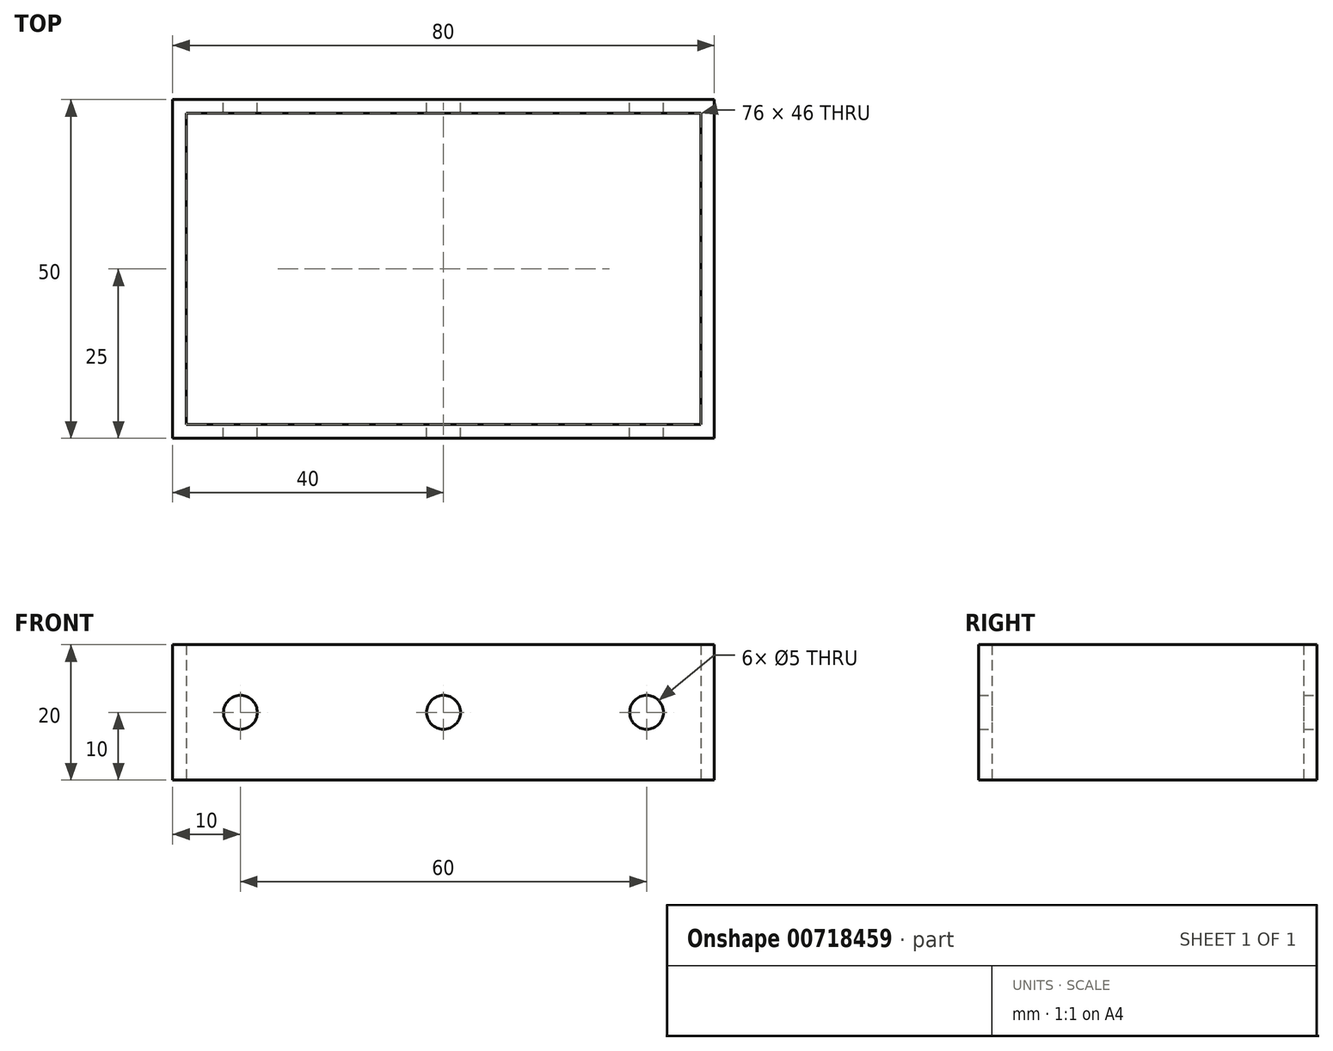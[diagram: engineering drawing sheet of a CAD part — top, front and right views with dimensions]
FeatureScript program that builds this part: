
annotation { "Feature Type Name" : "Feature", "Feature Type Description" : "" }
export const myFeature = defineFeature(function(context is Context, id is Id, definition is map)
    precondition{}
    {
        {
            var Q0;
            Q0=qCreatedBy(makeId("Top.planeOp"),FACE);
            var sketch = newSketch(context, id + "F0", { "sketchPlane" : qUnion([Q0])});
            skLineSegment(sketch, "E0.bottom", {"start": v(-40, 25) * mm, "end": v(40, 25) * mm});
            skLineSegment(sketch, "E0.top", {"start": v(-40, -25) * mm, "end": v(40, -25) * mm});
            skLineSegment(sketch, "E0.left", {"start": v(-40, 25) * mm, "end": v(-40, -25) * mm});
            skLineSegment(sketch, "E0.right", {"start": v(40, 25) * mm, "end": v(40, -25) * mm});
            skLineSegment(sketch, "E1.bottom", {"start": v(-38, 23) * mm, "end": v(38, 23) * mm});
            skLineSegment(sketch, "E1.top", {"start": v(-38, -23) * mm, "end": v(38, -23) * mm});
            skLineSegment(sketch, "E1.left", {"start": v(-38, 23) * mm, "end": v(-38, -23) * mm});
            skLineSegment(sketch, "E1.right", {"start": v(38, 23) * mm, "end": v(38, -23) * mm});
            skSolve(sketch);
        }
        {
            var Q0;
            Q0=makeQuery(id+"F0.imprint","IMPRINT",FACE,{"disambiguationData":[TD([[makeQuery(id+"F0.imprint","IMPRINT",EDGE,{"derivedFrom":sQuery(id+"F0.wireOp",EDGE,"E0.bottom")}),-1.0]])]});
            extrude(context, id + "F1", {"entities" : qUnion([Q0]), "depth" : 10 * mm, "offsetDistance" : 25 * mm, "hasSecondDirection" : true, "secondDirectionOppositeDirection" : true, "secondDirectionDepth" : 10 * mm});
        }
        {
            var Q0;
            Q0=qCreatedBy(makeId("Front.planeOp"),FACE);
            var sketch = newSketch(context, id + "F2", { "sketchPlane" : qUnion([Q0])});
            skCircle(sketch, "E2", {"center": v(0, 0) * mm, "radius": 2.5 * mm});
            skCircle(sketch, "E3", {"center": v(-30, 0) * mm, "radius": 2.5 * mm});
            skCircle(sketch, "E4", {"center": v(30, 0) * mm, "radius": 2.5 * mm});
            skSolve(sketch);
        }
        {
            var Q0;
            Q0=makeQuery(id+"F2.imprint","IMPRINT",FACE,{"disambiguationData":[TD([[makeQuery(id+"F2.imprint","IMPRINT",EDGE,{"derivedFrom":sQuery(id+"F2.wireOp",EDGE,"E3")}),1.0]])]});
            var Q1;
            Q1=makeQuery(id+"F2.imprint","IMPRINT",FACE,{"disambiguationData":[TD([[makeQuery(id+"F2.imprint","IMPRINT",EDGE,{"derivedFrom":sQuery(id+"F2.wireOp",EDGE,"E2")}),1.0]])]});
            var Q2;
            Q2=makeQuery(id+"F2.imprint","IMPRINT",FACE,{"disambiguationData":[TD([[makeQuery(id+"F2.imprint","IMPRINT",EDGE,{"derivedFrom":sQuery(id+"F2.wireOp",EDGE,"E4")}),1.0]])]});
            extrude(context, id + "F3", {"entities" : qUnion([Q0, Q1, Q2]), "operationType" : NewBodyOperationType.REMOVE, "depth" : 40 * mm, "offsetDistance" : 25 * mm, "hasSecondDirection" : true, "secondDirectionOppositeDirection" : true, "secondDirectionDepth" : 40 * mm});
        }
    });
